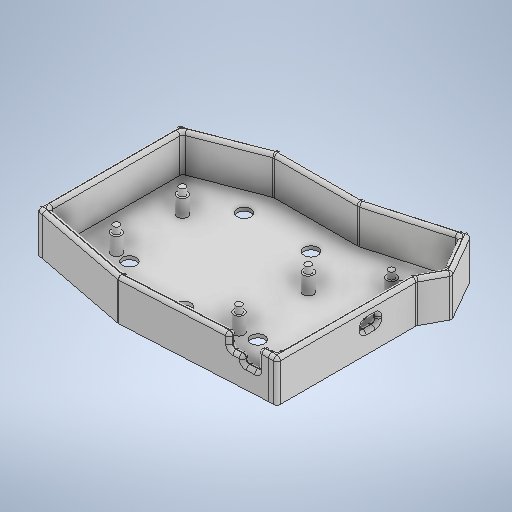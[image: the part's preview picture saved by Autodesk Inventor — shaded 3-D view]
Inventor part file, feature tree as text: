
AUTODESK INVENTOR PART (.ipt)
format: ipt  version: 2025 (Build 290162000, 162)  size: 555,008 bytes
history: native  units: mm
features: extrude x7, sketch x5, fillet x3, other x1
ambient origin geometry x8: Origin, YZ Plane, XZ Plane, XY Plane, X Axis, Y Axis, Z Axis, Center Point
bodies: Body1 (feature_tree)
feature tree (16):
  other  "Твердое тело1"
  sketch  "Эскиз1"
  sketch  "Эскиз2"
  sketch  "Эскиз3"
  extrude  "Выдавливание1"  Depth=2.0mm
  extrude  "Выдавливание2"  Depth=2.0mm
  extrude  "Выдавливание3"  Depth=5.0mm
  extrude  "Выдавливание4"  Depth=5.0mm
  extrude  "Выдавливание5"  Depth=6.0mm
  extrude  "Выдавливание8"  Depth=6.0mm
  extrude  "Выдавливание9"  Depth=6.0mm
  fillet  "Сопряжение2"  Radius=6.0mm
  fillet  "Сопряжение3"  Radius=6.0mm
  fillet  "Сопряжение4"  Radius=2.0mm
  sketch  "Эскиз6"
  sketch  "Эскиз7"
